# Revit family: Reece_Accessory_Milli_Inox_Shelf
name_source: partatom
category: Plumbing Fixtures
revit_build: Autodesk Revit 2018 (Build: 20190510_1515(x64)
units: mm (PartAtom-declared; Revit-internal decimal feet)

## family parameters
Cut with Voids When Loaded = Yes
Host = Face
Part Type = Normal
Room Calculation Point = Yes
Round Connector Dimension = Use Diameter
Shared = Yes

## types (1)
- Brushed Stainless Steel
    Default Elevation = 0 mm  [stored 0 ft]
    Description = Milli Inox Shelf Stainless Steel
    Disclaimer = THIS FILE IS THE PROPERTY OF THE REECE GROUP. IT MAY NOT BE REPRODUCED, REVERSE-ENGINEERED OR MODIFIED. ANY REPUBLICATION, TRANSMISSION OR DISTRIBUTION FOR THE PURPOSE OF COMMERCIALLY EXPLOITING THE FILES IS PROHIBITED.
    Keynote = Product #2259618, Reece_Accessory_Milli_Inox_Shelf - Brushed Stainless Steel
    Manufacturer = Milli
    Model = Inox
    Reece_Detail_Disclaimer = THIS FILE IS THE PROPERTY OF THE REECE GROUP. IT MAY NOT BE REPRODUCED, REVERSE-ENGINEERED OR MODIFIED. ANY REPUBLICATION, TRANSMISSION OR DISTRIBUTION FOR THE PURPOSE OF COMMERCIALLY EXPLOITING THE FILES IS PROHIBITED.
    Reece_Material_Main = Reece_Brass_Brushed Stainless Steel
    Reece_Overall_Length = 450 mm  [stored 1.47638 ft]
    Reece_Overall_Width = 120 mm  [stored 0.393701 ft]
    Reece_Product_Brand = Milli
    Reece_Product_Description = Milli Inox Shelf Stainless Steel
    Reece_Product_Mount = Wall Mounted
    Reece_Product_Number = 2259618
    Reece_Product_Sub Brand = Inox
    Reece_Product_Type = Accessory
    Reece_Product_Web Page = https://www.reece.com.au
    Type Comments = Accessory
    URL = https://www.reece.com.au

note: [stored X ft] marks values corroborated as IEEE doubles in the binary element streams (Revit-internal decimal feet)

## geometry (parser evidence)
native form markers: Sweep x3
no freeform markers — native parametric forms only
